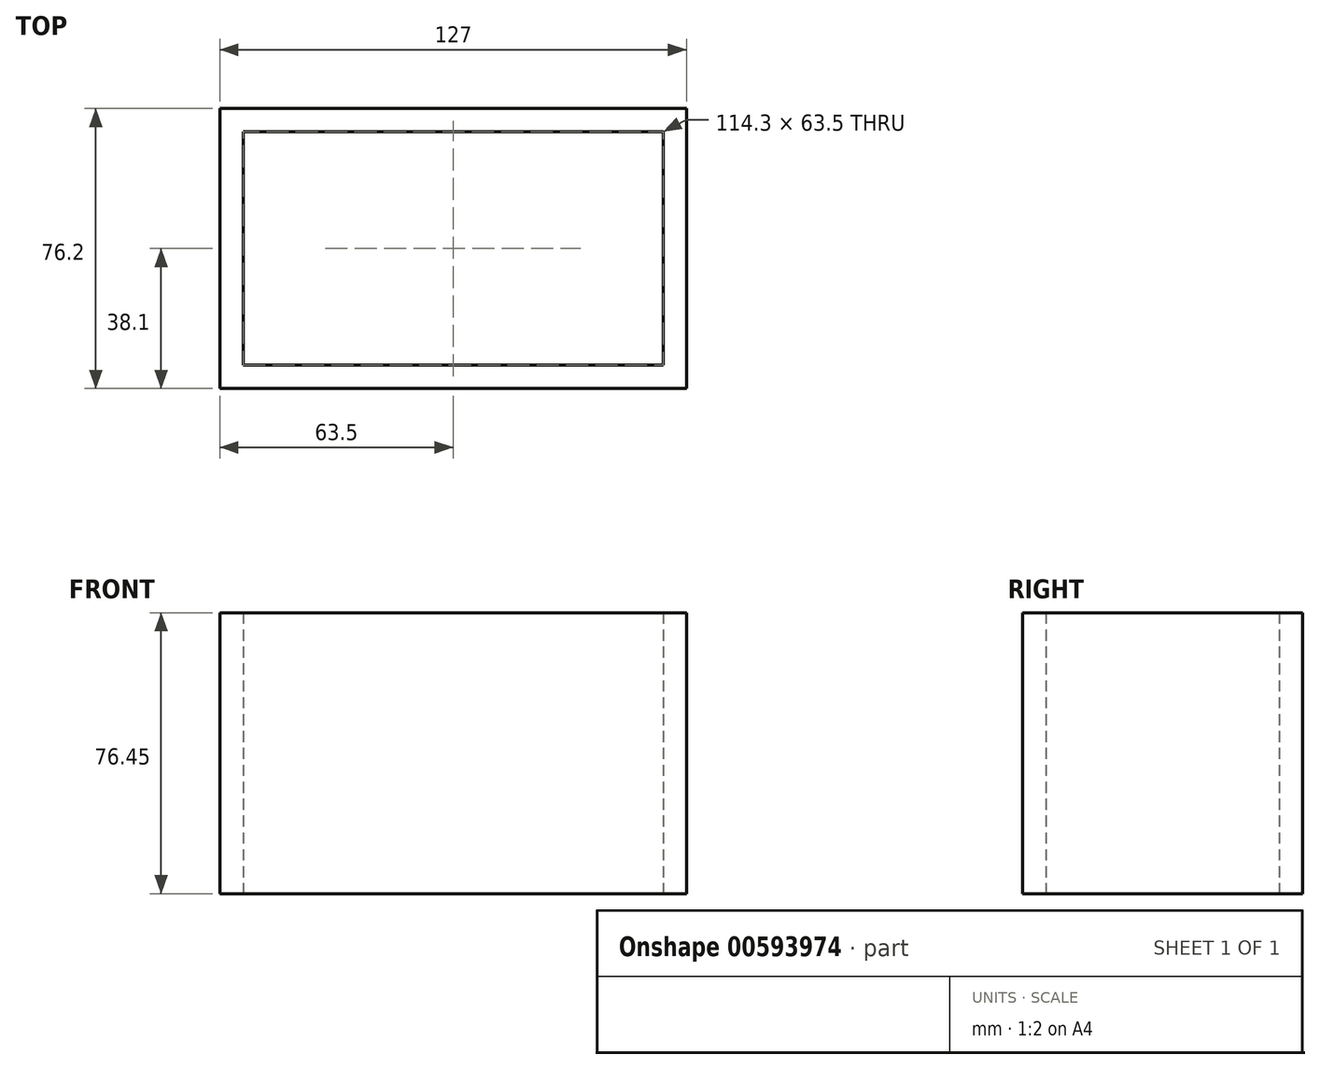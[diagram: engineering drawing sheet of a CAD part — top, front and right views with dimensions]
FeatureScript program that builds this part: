
annotation { "Feature Type Name" : "Feature", "Feature Type Description" : "" }
export const myFeature = defineFeature(function(context is Context, id is Id, definition is map)
    precondition{}
    {
        {
            var Q0;
            Q0=qCreatedBy(makeId("Top.planeOp"),FACE);
            var sketch = newSketch(context, id + "F0", { "sketchPlane" : qUnion([Q0])});
            skLineSegment(sketch, "E0.bottom", {"start": v(63.5, -38.1) * mm, "end": v(-63.5, -38.1) * mm});
            skLineSegment(sketch, "E0.top", {"start": v(63.5, 38.1) * mm, "end": v(-63.5, 38.1) * mm});
            skLineSegment(sketch, "E0.left", {"start": v(63.5, -38.1) * mm, "end": v(63.5, 38.1) * mm});
            skLineSegment(sketch, "E0.right", {"start": v(-63.5, -38.1) * mm, "end": v(-63.5, 38.1) * mm});
            skPoint(sketch, "E0.middle", {"position": v(0, 0) * mm});
            skLineSegment(sketch, "E1.0", {"start": v(57.15, 31.75) * mm, "end": v(-57.15, 31.75) * mm});
            skLineSegment(sketch, "E1.1", {"start": v(57.15, -31.75) * mm, "end": v(57.15, 31.75) * mm});
            skLineSegment(sketch, "E1.2", {"start": v(57.15, -31.75) * mm, "end": v(-57.15, -31.75) * mm});
            skLineSegment(sketch, "E1.3", {"start": v(-57.15, -31.75) * mm, "end": v(-57.15, 31.75) * mm});
            skSolve(sketch);
        }
        {
            var Q0;
            Q0 = qSketchRegion(id + "F0", true);
            extrude(context, id + "F1", {"entities" : qUnion([Q0]), "flatOperationType" : FlatOperationType.REMOVE, "depth" : 76.45 * mm, "offsetDistance" : 25.4 * mm, "domain" : OperationDomain.MODEL});
        }
    });
